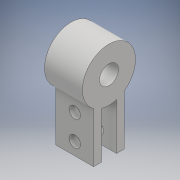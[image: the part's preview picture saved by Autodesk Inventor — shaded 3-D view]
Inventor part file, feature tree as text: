
AUTODESK INVENTOR PART (.ipt)
format: ipt  version: 2017 (Build 210142000, 142)  size: 130,560 bytes
history: native  units: mm
features: extrude x2, sketch x2
ambient origin geometry x8: Origin, YZ Plane, XZ Plane, XY Plane, X Axis, Y Axis, Z Axis, Center Point
bodies: Solid1 (feature_tree)
feature tree (4):
  extrude  "Extrusion1"  Depth=2.5mm
  extrude  "Extrusion2"  Depth=5.0mm
  sketch  "Sketch1"  dims[d0=7.0mm d1=2.5mm]
  sketch  "Sketch2"  dims[d2=1.0mm d3=6.0mm d4=5.0mm d5=0.0mm d6=1.5mm d7=1.5mm d8=5.0mm d9=0.0mm]
